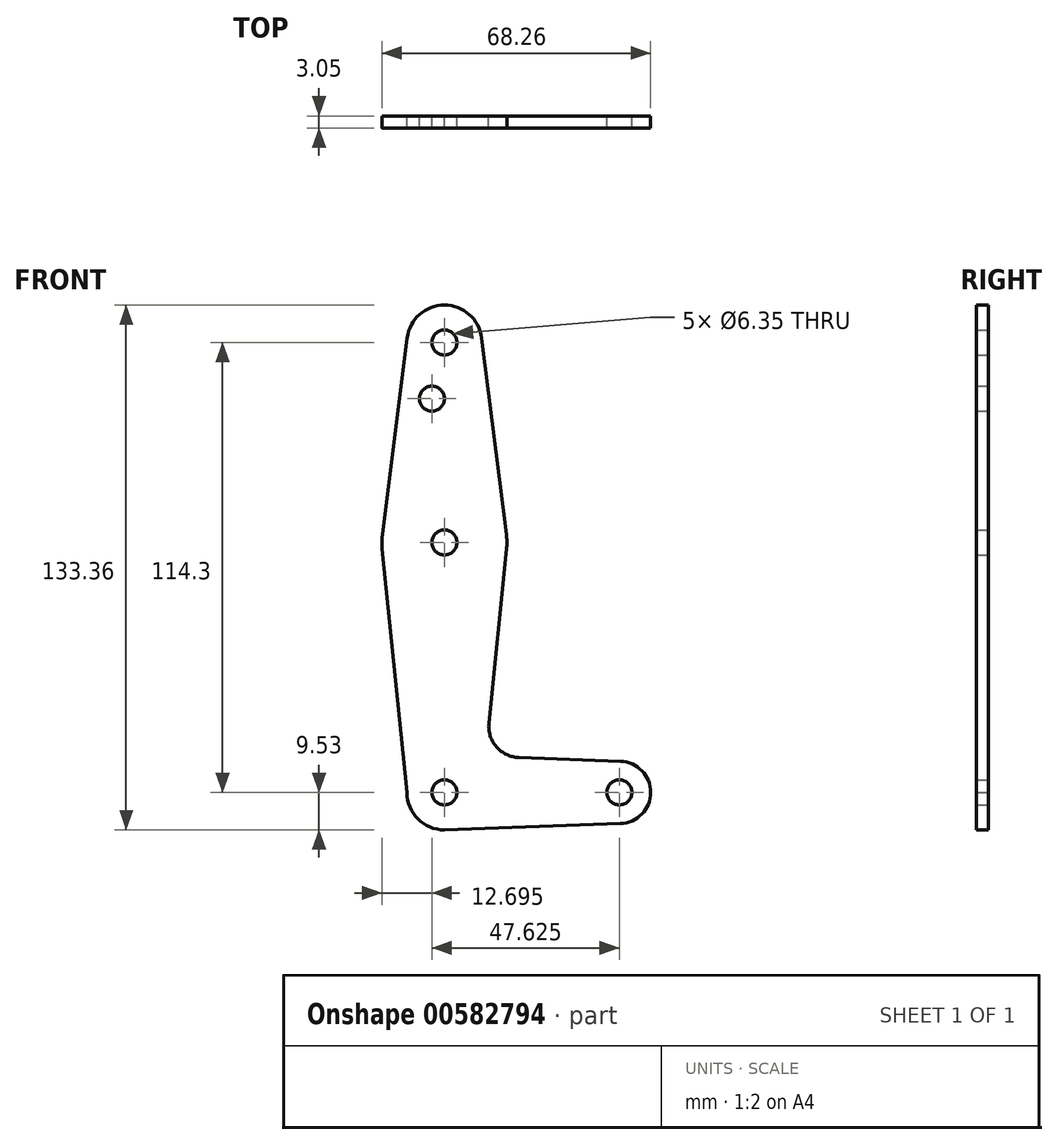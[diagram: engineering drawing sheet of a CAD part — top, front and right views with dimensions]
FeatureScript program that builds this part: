
annotation { "Feature Type Name" : "Feature", "Feature Type Description" : "" }
export const myFeature = defineFeature(function(context is Context, id is Id, definition is map)
    precondition{}
    {
        {
            var Q0;
            Q0=qCreatedBy(makeId("Front.planeOp"),FACE);
            var sketch = newSketch(context, id + "F0", { "sketchPlane" : qUnion([Q0])});
            skLineSegment(sketch, "E0", {"start": v(0, 0) * mm, "end": v(0, 114.3) * mm});
            skLineSegment(sketch, "E1", {"start": v(0, 0) * mm, "end": v(44.45, 0) * mm});
            skCircle(sketch, "E2", {"center": v(0, 114.3) * mm, "radius": 9.53 * mm});
            skCircle(sketch, "E3", {"center": v(0, 63.5) * mm, "radius": 15.88 * mm});
            skCircle(sketch, "E4", {"center": v(0, 0) * mm, "radius": 9.53 * mm});
            skCircle(sketch, "E5", {"center": v(44.45, 0) * mm, "radius": 7.94 * mm});
            skLineSegment(sketch, "E6", {"start": v(9.45, 115.5) * mm, "end": v(15.75, 65.48) * mm});
            skLineSegment(sketch, "E7", {"start": v(44.73, 7.93) * mm, "end": v(18.93, 8.85) * mm});
            skLineSegment(sketch, "E8", {"start": v(0, -9.52) * mm, "end": v(44.73, -7.93) * mm});
            skLineSegment(sketch, "E9", {"start": v(-15.76, 65.43) * mm, "end": v(-9.45, 115.5) * mm});
            skLineSegment(sketch, "E10", {"start": v(-9.53, 0) * mm, "end": v(-15.8, 61.9) * mm});
            skLineSegment(sketch, "E11", {"start": v(11.3, 17.6) * mm, "end": v(15.8, 61.9) * mm});
            skCircle(sketch, "E12", {"center": v(0, 114.3) * mm, "radius": 3.18 * mm});
            skCircle(sketch, "E13", {"center": v(0, 63.5) * mm, "radius": 3.18 * mm});
            skCircle(sketch, "E14", {"center": v(0, 0) * mm, "radius": 3.18 * mm});
            skCircle(sketch, "E15", {"center": v(44.45, 0) * mm, "radius": 3.18 * mm});
            skPoint(sketch, "E16.newPointB", {"position": v(0, 9.53) * mm});
            skArc(sketch, "E16.filletArc", {"start": v(11.3, 17.6) * mm, "mid": v(13.22, 11.57) * mm, "end": v(18.93, 8.85) * mm});
            skCircle(sketch, "E17", {"center": v(-3.18, 100.03) * mm, "radius": 3.18 * mm});
            skSolve(sketch);
        }
        {
            var Q0;
            {var subQ5=sQuery(id+"F0.wireOp",EDGE,"E10");Q0=makeQuery(id+"F0.imprint","IMPRINT",FACE,{"disambiguationData":[TD([[makeQuery(id+"F0.imprint","IMPRINT",EDGE,{"derivedFrom":subQ5}),-1.0]])]});}
            var Q1;
            {var subQ4=sQuery(id+"F0.wireOp",EDGE,"E7");Q1=makeQuery(id+"F0.imprint","IMPRINT",FACE,{"disambiguationData":[TD([[makeQuery(id+"F0.imprint","IMPRINT",EDGE,{"derivedFrom":subQ4}),1.0]])]});}
            var Q2;
            {var subQ4=sQuery(id+"F0.wireOp",EDGE,"E14");var subQ8=sQuery(id+"F0.wireOp",EDGE,"E0");var subQ10=makeQuery(id+"F0.imprint","INTERSECT",VERTEX,{"derivedFrom":[subQ8,subQ4]});Q2=makeQuery(id+"F0.imprint","IMPRINT",FACE,{"disambiguationData":[TD([[makeQuery(id+"F0.imprint","IMPRINT",EDGE,{"disambiguationData":[TD([[subQ10,-1.0]])],"derivedFrom":subQ8}),1.0]])]});}
            var Q3;
            {var subQ0=sQuery(id+"F0.wireOp",EDGE,"E14");var subQ1=sQuery(id+"F0.wireOp",EDGE,"E0");var subQ2=makeQuery(id+"F0.imprint","INTERSECT",VERTEX,{"derivedFrom":[subQ1,subQ0]});Q3=makeQuery(id+"F0.imprint","IMPRINT",FACE,{"disambiguationData":[TD([[makeQuery(id+"F0.imprint","IMPRINT",EDGE,{"disambiguationData":[TD([[subQ2,-1.0]])],"derivedFrom":subQ1}),-1.0]])]});}
            var Q4;
            {var subQ0=sQuery(id+"F0.wireOp",EDGE,"E5");var subQ1=sQuery(id+"F0.wireOp",EDGE,"E1");var subQ2=makeQuery(id+"F0.imprint","INTERSECT",VERTEX,{"derivedFrom":[subQ1,subQ0]});Q4=makeQuery(id+"F0.imprint","IMPRINT",FACE,{"disambiguationData":[TD([[makeQuery(id+"F0.imprint","IMPRINT",EDGE,{"disambiguationData":[TD([[subQ2,1.0]])],"derivedFrom":subQ1}),-1.0]])]});}
            var Q5;
            Q5=makeQuery(id+"F0.imprint","IMPRINT",FACE,{"disambiguationData":[TD([[makeQuery(id+"F0.imprint","IMPRINT",EDGE,{"derivedFrom":sQuery(id+"F0.wireOp",EDGE,"E15")}),-1.0]])]});
            var Q6;
            {var subQ0=sQuery(id+"F0.wireOp",EDGE,"E3");var subQ4=sQuery(id+"F0.wireOp",EDGE,"E0");var subQ7=makeQuery(id+"F0.imprint","INTERSECT",VERTEX,{"disambiguationData":[OD(0.0)],"derivedFrom":[subQ4,subQ0]});Q6=makeQuery(id+"F0.imprint","IMPRINT",FACE,{"disambiguationData":[TD([[makeQuery(id+"F0.imprint","IMPRINT",EDGE,{"disambiguationData":[TD([[subQ7,-1.0]])],"derivedFrom":subQ4}),1.0]])]});}
            var Q7;
            {var subQ0=sQuery(id+"F0.wireOp",EDGE,"E3");var subQ2=sQuery(id+"F0.wireOp",EDGE,"E0");var subQ4=makeQuery(id+"F0.imprint","INTERSECT",VERTEX,{"disambiguationData":[OD(0.0)],"derivedFrom":[subQ2,subQ0]});Q7=makeQuery(id+"F0.imprint","IMPRINT",FACE,{"disambiguationData":[TD([[makeQuery(id+"F0.imprint","IMPRINT",EDGE,{"disambiguationData":[TD([[subQ4,-1.0]])],"derivedFrom":subQ2}),-1.0]])]});}
            var Q8;
            {var subQ0=sQuery(id+"F0.wireOp",EDGE,"E6");Q8=makeQuery(id+"F0.imprint","IMPRINT",FACE,{"disambiguationData":[TD([[makeQuery(id+"F0.imprint","IMPRINT",EDGE,{"derivedFrom":subQ0}),-1.0]])]});}
            var Q9;
            {var subQ0=sQuery(id+"F0.wireOp",EDGE,"E9");Q9=makeQuery(id+"F0.imprint","IMPRINT",FACE,{"disambiguationData":[TD([[makeQuery(id+"F0.imprint","IMPRINT",EDGE,{"derivedFrom":subQ0}),-1.0]])]});}
            var Q10;
            Q10=makeQuery(id+"F0.imprint","IMPRINT",FACE,{"disambiguationData":[TD([[makeQuery(id+"F0.imprint","IMPRINT",EDGE,{"derivedFrom":sQuery(id+"F0.wireOp",EDGE,"E12")}),-1.0]])]});
            extrude(context, id + "F1", {"entities" : qUnion([Q0, Q1, Q2, Q3, Q4, Q5, Q6, Q7, Q8, Q9, Q10]), "depth" : 3.05 * mm, "offsetDistance" : 25.4 * mm});
        }
    });
